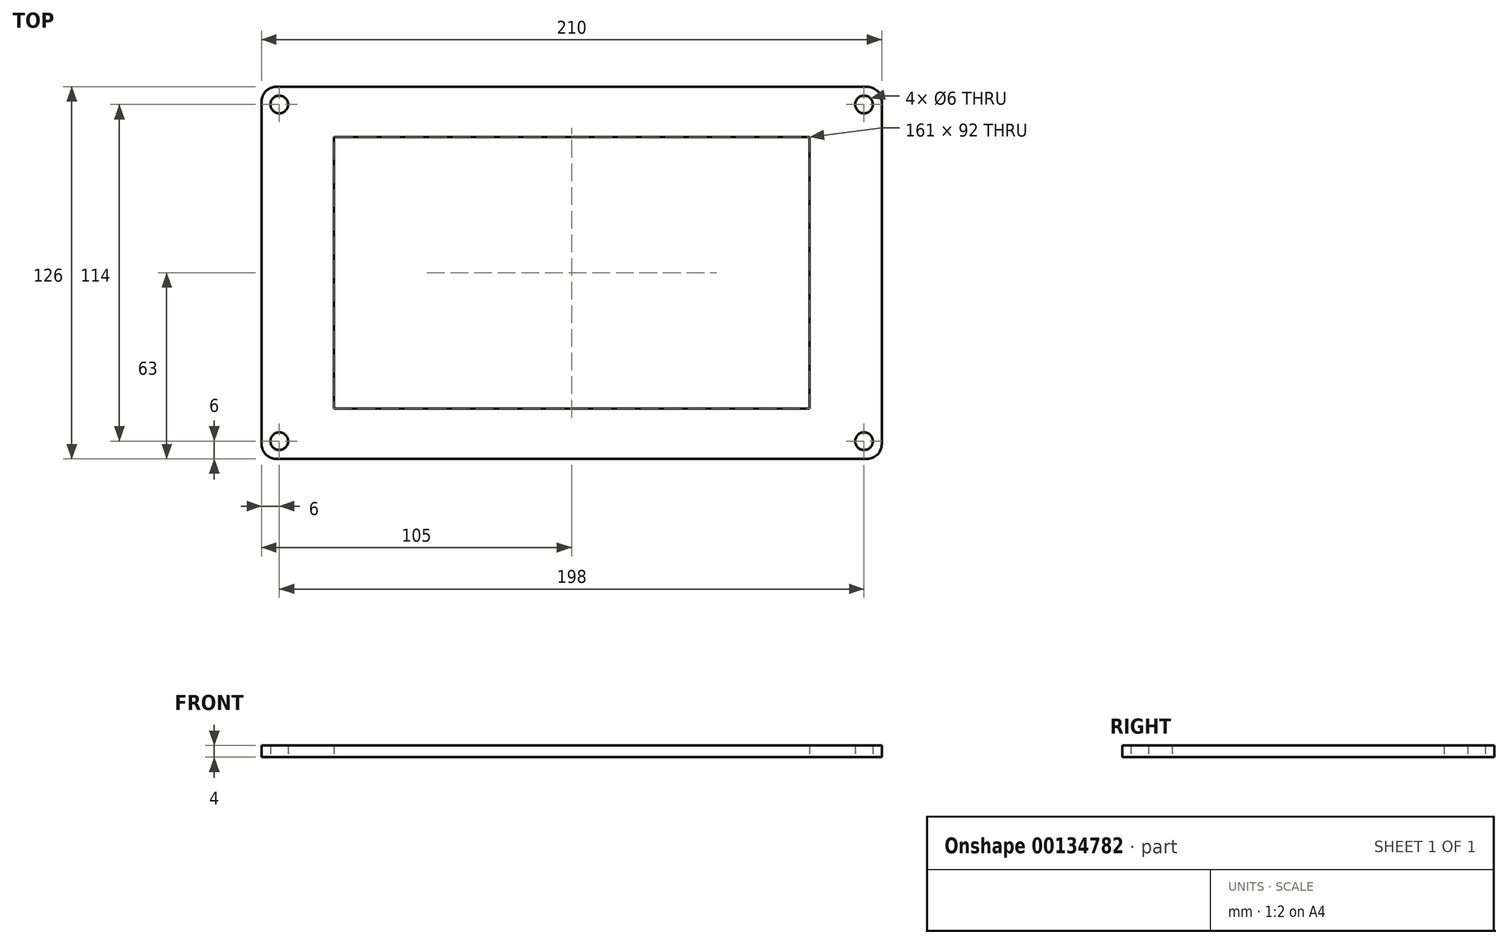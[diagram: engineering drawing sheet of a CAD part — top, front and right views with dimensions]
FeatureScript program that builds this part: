
annotation { "Feature Type Name" : "Feature", "Feature Type Description" : "" }
export const myFeature = defineFeature(function(context is Context, id is Id, definition is map)
    precondition{}
    {
        {
            var Q0;
            Q0=qCreatedBy(makeId("Top.planeOp"),FACE);
            var sketch = newSketch(context, id + "F0", { "sketchPlane" : qUnion([Q0])});
            skLineSegment(sketch, "E0.bottom", {"start": v(92, 55) * mm, "end": v(-92, 55) * mm, "construction": true});
            skLineSegment(sketch, "E0.top", {"start": v(92, -55) * mm, "end": v(-92, -55) * mm, "construction": true});
            skLineSegment(sketch, "E0.left", {"start": v(97, 50) * mm, "end": v(97, -50) * mm, "construction": true});
            skLineSegment(sketch, "E0.right", {"start": v(-97, 50) * mm, "end": v(-97, -50) * mm, "construction": true});
            skPoint(sketch, "E0.middle", {"position": v(0, 0) * mm});
            skLineSegment(sketch, "E1.bottom", {"start": v(77.5, 43) * mm, "end": v(-77.5, 43) * mm, "construction": true});
            skLineSegment(sketch, "E1.top", {"start": v(77.5, -43) * mm, "end": v(-77.5, -43) * mm, "construction": true});
            skLineSegment(sketch, "E1.left", {"start": v(77.5, 43) * mm, "end": v(77.5, -43) * mm, "construction": true});
            skLineSegment(sketch, "E1.right", {"start": v(-77.5, 43) * mm, "end": v(-77.5, -43) * mm, "construction": true});
            skPoint(sketch, "E2.visualSharp", {"position": v(-97, 55) * mm});
            skArc(sketch, "E2.filletArc", {"start": v(-92, 55) * mm, "mid": v(-95.54, 53.54) * mm, "end": v(-97, 50) * mm, "construction": true});
            skPoint(sketch, "E3.visualSharp", {"position": v(97, 55) * mm});
            skArc(sketch, "E3.filletArc", {"start": v(97, 50) * mm, "mid": v(95.54, 53.54) * mm, "end": v(92, 55) * mm, "construction": true});
            skPoint(sketch, "E4.visualSharp", {"position": v(97, -55) * mm});
            skArc(sketch, "E4.filletArc", {"start": v(92, -55) * mm, "mid": v(95.54, -53.54) * mm, "end": v(97, -50) * mm, "construction": true});
            skPoint(sketch, "E5.visualSharp", {"position": v(-97, -55) * mm});
            skArc(sketch, "E5.filletArc", {"start": v(-97, -50) * mm, "mid": v(-95.54, -53.54) * mm, "end": v(-92, -55) * mm, "construction": true});
            skSolve(sketch);
        }
        {
            var Q0;
            Q0=qCreatedBy(makeId("Top.planeOp"),FACE);
            var sketch = newSketch(context, id + "F1", { "sketchPlane" : qUnion([Q0])});
            skLineSegment(sketch, "E6.bottom", {"start": v(100, 63) * mm, "end": v(-100, 63) * mm});
            skLineSegment(sketch, "E6.top", {"start": v(100, -63) * mm, "end": v(-100, -63) * mm});
            skLineSegment(sketch, "E6.left", {"start": v(105, 58) * mm, "end": v(105, -58) * mm});
            skLineSegment(sketch, "E6.right", {"start": v(-105, 58) * mm, "end": v(-105, -58) * mm});
            skPoint(sketch, "E6.middle", {"position": v(0, 0) * mm});
            skLineSegment(sketch, "E7.bottom", {"start": v(80.5, 46) * mm, "end": v(-80.5, 46) * mm});
            skLineSegment(sketch, "E7.top", {"start": v(80.5, -46) * mm, "end": v(-80.5, -46) * mm});
            skLineSegment(sketch, "E7.left", {"start": v(80.5, 46) * mm, "end": v(80.5, -46) * mm});
            skLineSegment(sketch, "E7.right", {"start": v(-80.5, 46) * mm, "end": v(-80.5, -46) * mm});
            skCircle(sketch, "E8", {"center": v(-99, 57) * mm, "radius": 3 * mm});
            skCircle(sketch, "E9.0.1.0", {"center": v(-99, -57) * mm, "radius": 3 * mm});
            skCircle(sketch, "E9.1.0.0", {"center": v(99, 57) * mm, "radius": 3 * mm});
            skCircle(sketch, "E9.1.1.0", {"center": v(99, -57) * mm, "radius": 3 * mm});
            skLineSegment(sketch, "E9.direction1", {"start": v(-99, 57) * mm, "end": v(99, 57) * mm, "construction": true});
            skLineSegment(sketch, "E9.direction2", {"start": v(-99, 57) * mm, "end": v(-99, -57) * mm, "construction": true});
            skPoint(sketch, "E10.visualSharp", {"position": v(-105, 63) * mm});
            skArc(sketch, "E10.filletArc", {"start": v(-100, 63) * mm, "mid": v(-103.54, 61.54) * mm, "end": v(-105, 58) * mm});
            skPoint(sketch, "E11.visualSharp", {"position": v(-105, -63) * mm});
            skArc(sketch, "E11.filletArc", {"start": v(-105, -58) * mm, "mid": v(-103.54, -61.54) * mm, "end": v(-100, -63) * mm});
            skPoint(sketch, "E12.visualSharp", {"position": v(105, -63) * mm});
            skArc(sketch, "E12.filletArc", {"start": v(100, -63) * mm, "mid": v(103.54, -61.54) * mm, "end": v(105, -58) * mm});
            skPoint(sketch, "E13.visualSharp", {"position": v(105, 63) * mm});
            skArc(sketch, "E13.filletArc", {"start": v(105, 58) * mm, "mid": v(103.54, 61.54) * mm, "end": v(100, 63) * mm});
            skSolve(sketch);
        }
        {
            var Q0;
            Q0=makeQuery(id+"F1.imprint","IMPRINT",FACE,{"disambiguationData":[TD([[makeQuery(id+"F1.imprint","IMPRINT",EDGE,{"derivedFrom":sQuery(id+"F1.wireOp",EDGE,"E6.bottom")}),1.0]])]});
            extrude(context, id + "F2", {"entities" : qUnion([Q0]), "depth" : 4 * mm});
        }
    });
